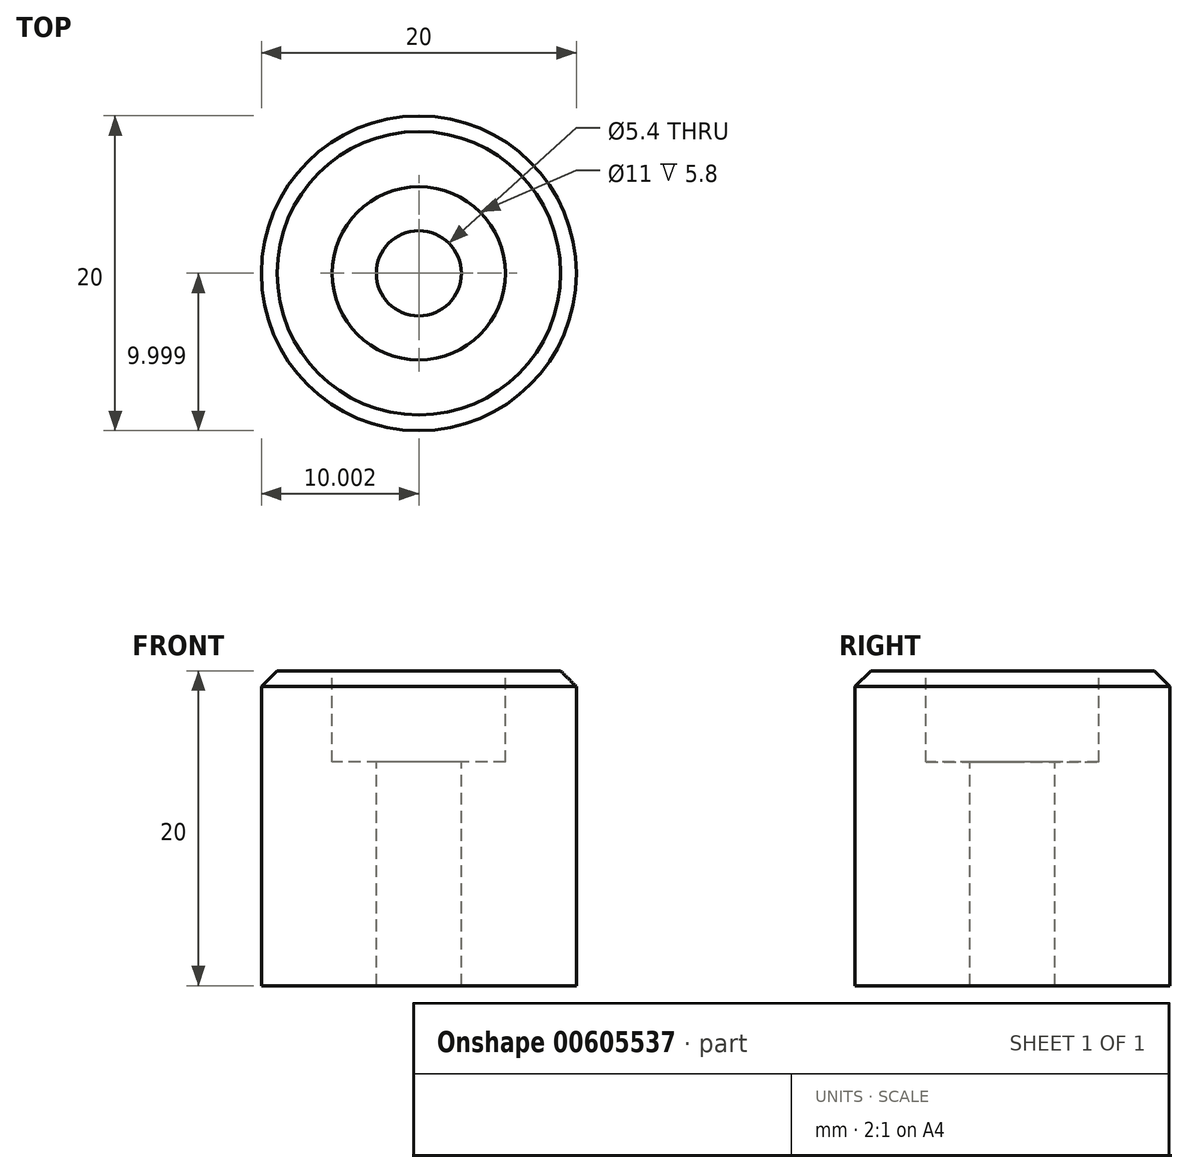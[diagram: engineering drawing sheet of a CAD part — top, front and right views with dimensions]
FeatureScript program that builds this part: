
annotation { "Feature Type Name" : "Feature", "Feature Type Description" : "" }
export const myFeature = defineFeature(function(context is Context, id is Id, definition is map)
    precondition{}
    {
        {
            var Q0;
            Q0=qCreatedBy(makeId("Top.planeOp"),FACE);
            var sketch = newSketch(context, id + "F0", { "sketchPlane" : qUnion([Q0])});
            skCircle(sketch, "E0", {"center": v(-63.56, 20.24) * mm, "radius": 10 * mm});
            skSolve(sketch);
        }
        {
            var Q0;
            Q0 = qSketchRegion(id + "F0", true);
            extrude(context, id + "F1", {"entities" : qUnion([Q0]), "depth" : 20 * mm, "offsetDistance" : 25 * mm});
        }
        {
            var Q0;
            Q0=makeQuery(id+"F1.opExtrude","CAP_EDGE",EDGE,{"disambiguationData":[OSD([sQuery(id+"F0.wireOp",EDGE,"E0")])],"isStart":false});
            chamfer(context, id + "F2", {"entities" : qUnion([Q0]), "width" : 1 * mm, "tangentPropagation" : true});
        }
        {
            var Q0;
            Q0=makeQuery(id+"F1.opExtrude","CAP_FACE",FACE,{"disambiguationData":[OSD([sQuery(id+"F0.wireOp",EDGE,"E0")])],"isStart":false});
            var sketch = newSketch(context, id + "F3", { "sketchPlane" : qUnion([Q0])});
            skPoint(sketch, "E1", {"position": v(-63.56, 20.24) * mm});
            skSolve(sketch);
        }
        {
            var Q0;
            Q0=sQuery(id+"F3.wireOp",VERTEX,"E1");
            var Q1;
            Q1=makeQuery(id+"F1.opExtrude","SWEPT_BODY",BODY,{"disambiguationData":[OSD([sQuery(id+"F0.wireOp",EDGE,"E0")])]});
            hole(context, id + "F4", {"style" : HoleStyle.C_BORE, "endStyle" : HoleEndStyle.THROUGH, "holeDiameter" : 5.4 * mm, "cBoreDiameter" : 11 * mm, "cBoreDepth" : 5.8 * mm, "majorDiameter" : 6 * mm, "tappedDepth" : 12 * mm, "tapClearance" : 3, "locations" : qUnion([Q0]), "scope" : qUnion([Q1])});
        }
    });
